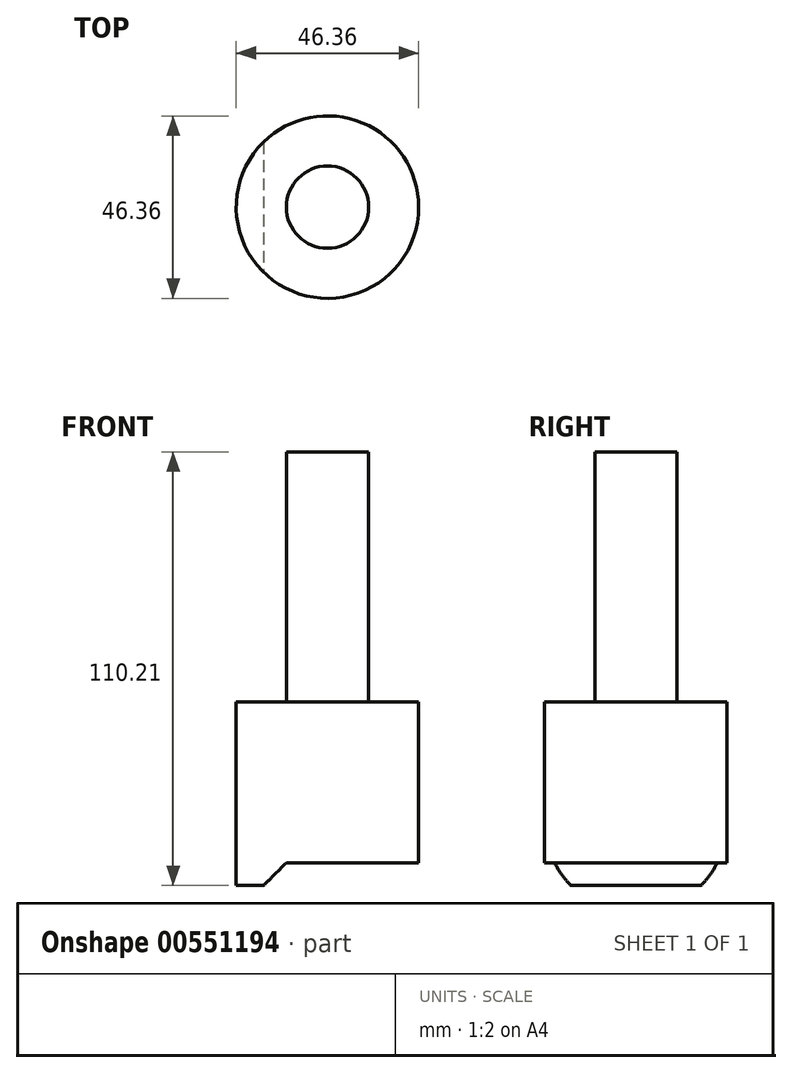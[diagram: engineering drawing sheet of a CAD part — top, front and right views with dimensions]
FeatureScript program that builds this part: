
annotation { "Feature Type Name" : "Feature", "Feature Type Description" : "" }
export const myFeature = defineFeature(function(context is Context, id is Id, definition is map)
    precondition{}
    {
        {
            var Q0;
            Q0=qCreatedBy(makeId("Top.planeOp"),FACE);
            var sketch = newSketch(context, id + "F0", { "sketchPlane" : qUnion([Q0])});
            skCircle(sketch, "E0", {"center": v(0, 0) * mm, "radius": 23.18 * mm});
            skSolve(sketch);
        }
        {
            var Q0;
            Q0 = qSketchRegion(id + "F0", true);
            extrude(context, id + "F1", {"entities" : qUnion([Q0]), "depth" : 46.7 * mm, "offsetDistance" : 25.4 * mm});
        }
        {
            var Q0;
            Q0=makeQuery(id+"F1.opExtrude","CAP_FACE",FACE,{"disambiguationData":[OSD([sQuery(id+"F0.wireOp",EDGE,"E0")])],"isStart":false});
            var sketch = newSketch(context, id + "F2", { "sketchPlane" : qUnion([Q0])});
            skCircle(sketch, "E1", {"center": v(0, 0) * mm, "radius": 10.46 * mm});
            skSolve(sketch);
        }
        {
            var Q0;
            Q0 = qSketchRegion(id + "F2", true);
            extrude(context, id + "F3", {"entities" : qUnion([Q0]), "operationType" : NewBodyOperationType.ADD, "depth" : 63.5 * mm, "offsetDistance" : 25.4 * mm});
        }
        {
            var Q0;
            Q0=qCreatedBy(makeId("Front.planeOp"),FACE);
            var sketch = newSketch(context, id + "F4", { "sketchPlane" : qUnion([Q0])});
            skLineSegment(sketch, "E2", {"start": v(-16.28, 0) * mm, "end": v(-10.46, 5.82) * mm});
            skLineSegment(sketch, "E3", {"start": v(-10.46, 5.82) * mm, "end": v(23.18, 5.82) * mm});
            skLineSegment(sketch, "E4", {"start": v(23.18, 5.82) * mm, "end": v(23.18, 0) * mm});
            skLineSegment(sketch, "E5", {"start": v(23.18, 0) * mm, "end": v(-16.28, 0) * mm});
            skLineSegment(sketch, "E6", {"start": v(12.7, -58.28) * mm, "end": v(12.7, -4.2) * mm});
            skLineSegment(sketch, "E7", {"start": v(10.45, -1.95) * mm, "end": v(-10.45, -1.95) * mm});
            skLineSegment(sketch, "E8", {"start": v(-12.7, -4.2) * mm, "end": v(-12.7, -59.87) * mm});
            skLineSegment(sketch, "E9", {"start": v(12.7, -4.2) * mm, "end": v(10.45, -1.95) * mm});
            skLineSegment(sketch, "E10", {"start": v(-10.45, -1.95) * mm, "end": v(-12.7, -4.2) * mm});
            skSolve(sketch);
        }
        {
            var Q0;
            Q0 = qSketchRegion(id + "F4", true);
            extrude(context, id + "F5", {"entities" : qUnion([Q0]), "operationType" : NewBodyOperationType.REMOVE, "endBound" : BoundingType.THROUGH_ALL, "oppositeDirection" : true, "depth" : 25.4 * mm, "offsetDistance" : 25.4 * mm, "hasSecondDirection" : true, "secondDirectionBound" : SecondDirectionBoundingType.THROUGH_ALL, "secondDirectionOppositeDirection" : false, "secondDirectionDepth" : 25.4 * mm});
        }
    });
